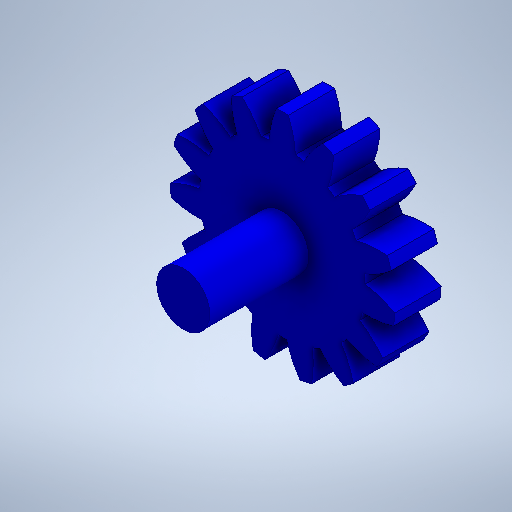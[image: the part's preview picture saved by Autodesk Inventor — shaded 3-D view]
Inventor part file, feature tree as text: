
AUTODESK INVENTOR PART (.ipt)
format: ipt  version: 2025.2 (Build 292293000, 293)  size: 378,880 bytes
history: native  units: mm (DEFAULTED — no unit token found)
features: plane x3, other x3, extrude x2, sketch x2
ambient origin geometry x8: Origin, YZ Plane, XZ Plane, XY Plane, X Axis, Y Axis, Z Axis, Center Point
bodies: Solid1 (feature_tree)
feature tree (10):
  extrude  "Extrusion1"  Depth=7.0mm TaperAngle=0.0deg
  plane  "Work Plane2"
  plane  "Work Plane8"
  plane  "Work Plane9"
  other  "Spur Gear"
  extrude  "Extrusion2"  Depth=10.0mm TaperAngle=0.0deg
  sketch  "Sketch1"  dims[d0=34.0mm d1=7.0mm d2=0.0mm]
  other  "Srf1"
  sketch  "Sketch3"  dims[d3=30.0mm d4=10.0mm d5=0.0mm d16=60.0mm d17=0.0mm d34=2.094395mm d39=0.0mm d41=0.0mm d43=60.0mm d46=60.0mm d47=0.0mm d48=0.0mm d49=8.0mm d50=15.0mm d51=0.0mm]
  other  "Pitch Diameter"
